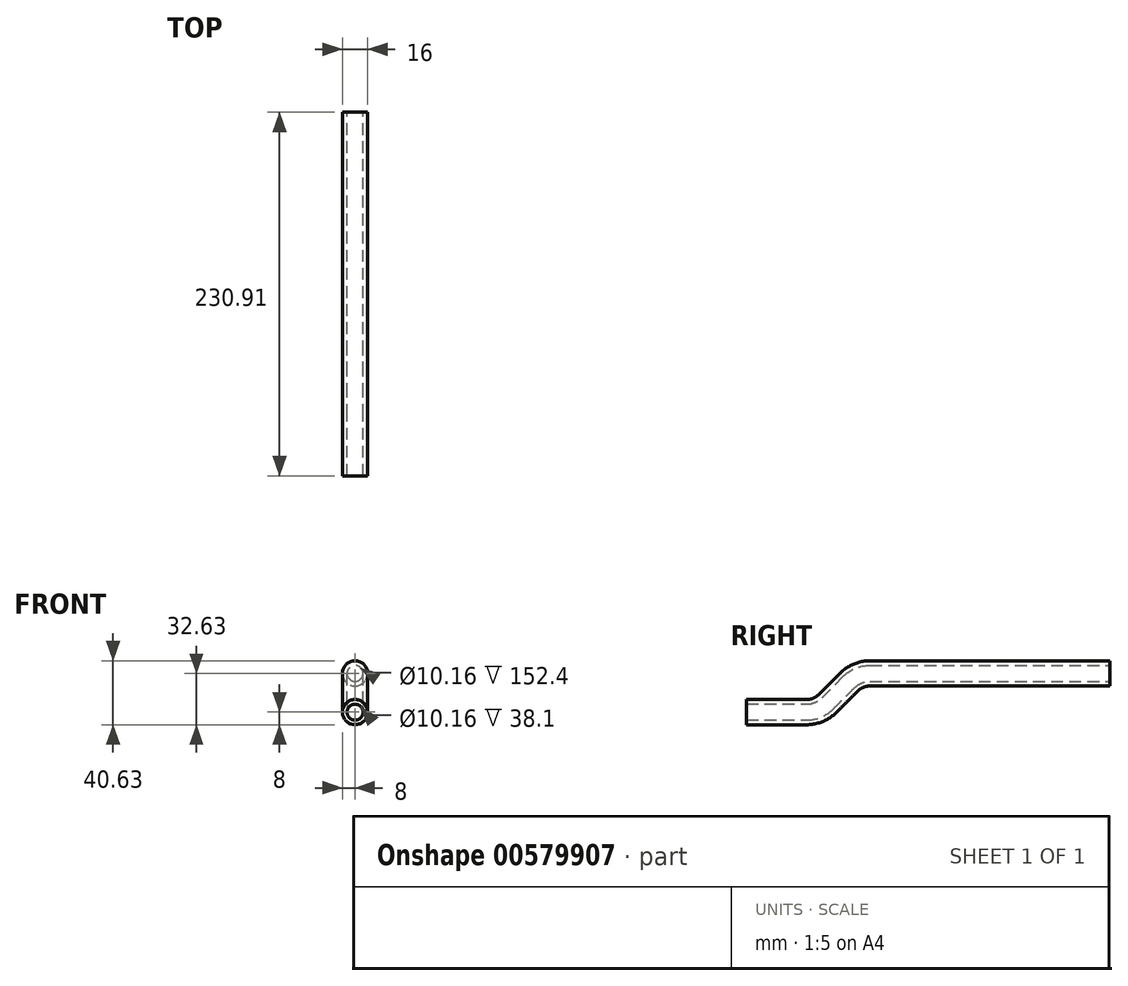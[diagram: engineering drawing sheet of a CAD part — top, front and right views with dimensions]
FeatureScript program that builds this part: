
annotation { "Feature Type Name" : "Feature", "Feature Type Description" : "" }
export const myFeature = defineFeature(function(context is Context, id is Id, definition is map)
    precondition{}
    {
        {
            var Q0;
            Q0=qCreatedBy(makeId("Front.planeOp"),FACE);
            var sketch = newSketch(context, id + "F0", { "sketchPlane" : qUnion([Q0])});
            skCircle(sketch, "E0", {"center": v(0, 0) * mm, "radius": 8 * mm});
            skCircle(sketch, "E1", {"center": v(0, 0) * mm, "radius": 5.08 * mm});
            skSolve(sketch);
        }
        {
            var Q0;
            Q0=qSketchRegion(id+"F0",true);
            extrude(context, id + "F1", {"entities" : qUnion([Q0]), "depth" : 152.4 * mm, "offsetDistance" : 25.4 * mm});
        }
        {
            var Q0;
            Q0=makeQuery(id+"F1.opExtrude","CAP_FACE",FACE,{"disambiguationData":[OSD([sQuery(id+"F0.wireOp",EDGE,"E0"),sQuery(id+"F0.wireOp",EDGE,"E1")])],"isStart":false});
            var sketch = newSketch(context, id + "F2", { "sketchPlane" : qUnion([Q0])});
            skCircle(sketch, "E2", {"center": v(0, 0) * mm, "radius": 8 * mm});
            skCircle(sketch, "E3", {"center": v(0, 0) * mm, "radius": 5.08 * mm});
            skLineSegment(sketch, "E4", {"start": v(-9.24, -19.05) * mm, "end": v(12.9, -19.05) * mm});
            skSolve(sketch);
        }
        {
            var Q0;
            Q0 = qSketchRegion(id + "F2", true);
            var Q1;
            Q1=sQuery(id+"F2.wireOp",EDGE,"E4");
            revolve(context, id + "F3", {"operationType" : NewBodyOperationType.ADD, "entities" : qUnion([Q0]), "axis" : qUnion([Q1]), "revolveType" : RevolveType.ONE_DIRECTION, "angle" : 45 * degree});
        }
        {
            var Q0;
            Q0=makeQuery(id+"F3.opRevolve","CAP_FACE",FACE,{"disambiguationData":[OSD([sQuery(id+"F2.wireOp",EDGE,"E2"),sQuery(id+"F2.wireOp",EDGE,"E3")])],"isStart":false});
            var sketch = newSketch(context, id + "F4", { "sketchPlane" : qUnion([Q0])});
            skCircle(sketch, "E5", {"center": v(0, 113.34) * mm, "radius": 8 * mm});
            skCircle(sketch, "E6", {"center": v(0, 113.34) * mm, "radius": 5.08 * mm});
            skSolve(sketch);
        }
        {
            var Q0;
            Q0 = qSketchRegion(id + "F4", true);
            extrude(context, id + "F5", {"entities" : qUnion([Q0]), "operationType" : NewBodyOperationType.ADD, "depth" : 19.05 * mm, "offsetDistance" : 25.4 * mm});
        }
        {
            var Q0;
            Q0=makeQuery(id+"F5.opExtrude","CAP_FACE",FACE,{"disambiguationData":[OSD([sQuery(id+"F4.wireOp",EDGE,"E5"),sQuery(id+"F4.wireOp",EDGE,"E6")])],"isStart":false});
            var sketch = newSketch(context, id + "F6", { "sketchPlane" : qUnion([Q0])});
            skCircle(sketch, "E7", {"center": v(0, 113.34) * mm, "radius": 8 * mm});
            skCircle(sketch, "E8", {"center": v(0, 113.34) * mm, "radius": 5.08 * mm});
            skLineSegment(sketch, "E9", {"start": v(-10.63, 132.4) * mm, "end": v(11.78, 132.4) * mm});
            skSolve(sketch);
        }
        {
            var Q0;
            Q0 = qSketchRegion(id + "F6", true);
            var Q1;
            Q1=sQuery(id+"F6.wireOp",EDGE,"E9");
            revolve(context, id + "F7", {"operationType" : NewBodyOperationType.ADD, "entities" : qUnion([Q0]), "axis" : qUnion([Q1]), "revolveType" : RevolveType.ONE_DIRECTION, "oppositeDirection" : true, "angle" : 45 * degree});
        }
        {
            var Q0;
            Q0=makeQuery(id+"F7.opRevolve","CAP_FACE",FACE,{"disambiguationData":[OSD([sQuery(id+"F6.wireOp",EDGE,"E7"),sQuery(id+"F6.wireOp",EDGE,"E8")])],"isStart":false});
            var sketch = newSketch(context, id + "F8", { "sketchPlane" : qUnion([Q0])});
            skCircle(sketch, "E10", {"center": v(0, -24.63) * mm, "radius": 8 * mm});
            skCircle(sketch, "E11", {"center": v(0, -24.63) * mm, "radius": 5.08 * mm});
            skSolve(sketch);
        }
        {
            var Q0;
            Q0 = qSketchRegion(id + "F8", true);
            extrude(context, id + "F9", {"entities" : qUnion([Q0]), "operationType" : NewBodyOperationType.ADD, "depth" : 38.1 * mm, "offsetDistance" : 25.4 * mm});
        }
    });
